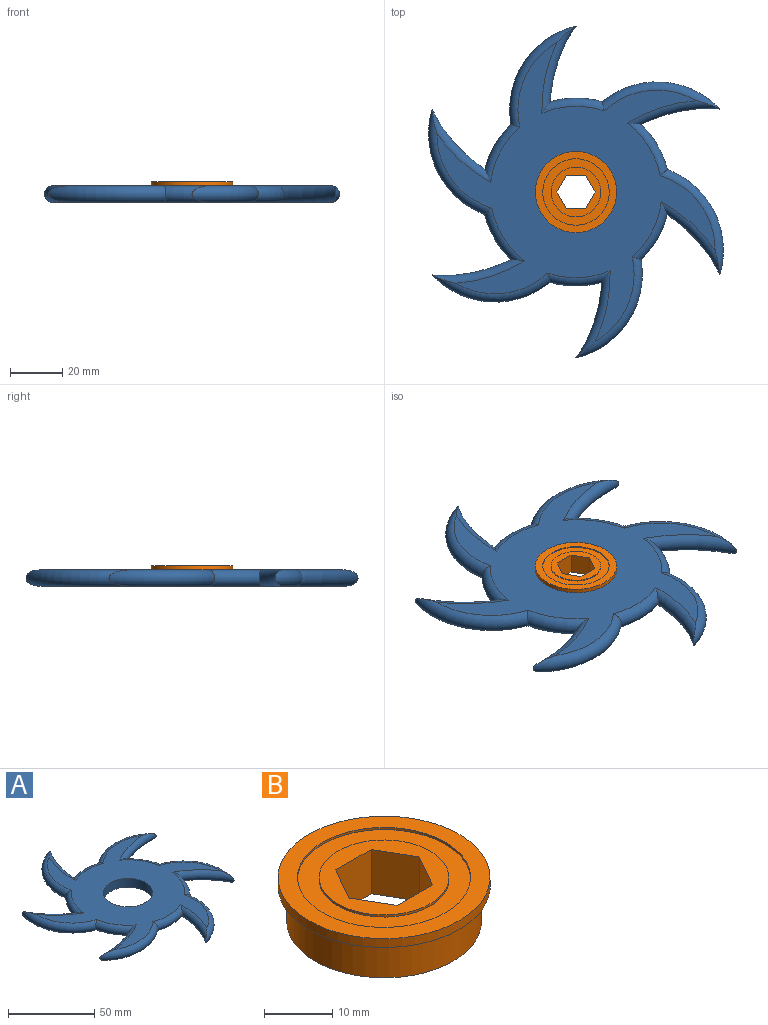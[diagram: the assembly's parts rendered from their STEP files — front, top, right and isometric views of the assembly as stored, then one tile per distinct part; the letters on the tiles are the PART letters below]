
ASSEMBLY  parts=2 mates=1
PART A: 21 faces, bbox 128.9x138.9x6.4 mm
  f0: cylinder r=14.29mm len=28.58mm, axis (0,0,-1), area 570mm2, adj f1,f2
  f1: plane 114.48x106.44mm, normal (0,0,1), area 3978.2mm2, adj f0,f3,f4,f5,f6,f7,f8,f9
  f2: plane 114.48x106.44mm, normal (0,0,-1), area 3978.2mm2, adj f0,f3,f4,f5,f6,f7,f8,f9
  f3: torus R=32.81mm, axis (0,0,1), area 216mm2, adj f1,f2,f4,f5
  f4: torus R=58.98mm, axis (0,0,1), area 299.1mm2, adj f1,f2,f3,f6
  f5: torus R=29.76mm, axis (0,0,1), area 453.4mm2, adj f1,f2,f3,f7
  f6: torus R=29.76mm, axis (0,0,1), area 453.4mm2, adj f1,f2,f4,f8
  f7: torus R=58.98mm, axis (0,0,1), area 299.1mm2, adj f1,f2,f5,f9
  f8: torus R=32.81mm, axis (0,0,1), area 216mm2, adj f1,f2,f6,f10
  f9: torus R=32.81mm, axis (0,0,1), area 216mm2, adj f1,f2,f7,f11
  f10: torus R=58.98mm, axis (0,0,1), area 299.1mm2, adj f1,f2,f8,f12
  f11: torus R=29.76mm, axis (0,0,1), area 453.4mm2, adj f1,f2,f9,f13
  f12: torus R=29.76mm, axis (0,0,1), area 453.4mm2, adj f1,f2,f10,f14
  f13: torus R=58.98mm, axis (0,0,1), area 299.1mm2, adj f1,f2,f11,f15
  f14: torus R=32.81mm, axis (0,0,1), area 216mm2, adj f1,f2,f12,f16
  f15: torus R=32.81mm, axis (0,0,1), area 216mm2, adj f1,f2,f13,f17
  f16: torus R=58.98mm, axis (0,0,1), area 299.1mm2, adj f1,f2,f14,f18
  f17: torus R=29.76mm, axis (0,0,1), area 453.4mm2, adj f1,f2,f15,f19
  f18: torus R=29.76mm, axis (0,0,1), area 453.4mm2, adj f1,f2,f16,f20
  f19: torus R=58.98mm, axis (0,0,1), area 299.1mm2, adj f1,f2,f17,f20
  f20: torus R=32.81mm, axis (0,0,1), area 216mm2, adj f1,f2,f18,f19
PART B: 15 faces, bbox 31.1x31.1x7.9 mm
  f0: cylinder r=12.7mm len=25.4mm, axis (0,0,1), area 30.4mm2, adj f7,f8
  f1: cylinder r=15.56mm len=31.12mm, axis (0,0,1), area 155.2mm2, adj f6,f7
  f2: cylinder r=14.27mm len=28.55mm, axis (0,0,1), area 569.5mm2, adj f5,f6
  f3: cylinder r=9.53mm len=19.05mm, axis (0,0,1), area 22.8mm2, adj f4,f8
  f4: plane 19.05x19.05mm, normal (0,0,1), area 144.9mm2, adj f3,f9,f10,f11,f12,f13,f14
  f5: plane 28.55x28.55mm, normal (0,0,-1), area 500mm2, adj f2,f9,f10,f11,f12,f13,f14
  f6: plane 31.12x31.12mm, normal (0,0,-1), area 120.2mm2, adj f1,f2
  f7: plane 31.12x31.12mm, normal (0,0,1), area 253.7mm2, adj f0,f1
  f8: plane 25.4x25.4mm, normal (0,0,1), area 221.7mm2, adj f0,f3
  f9: plane 7.94x6.36mm, normal (-0.87,-0.5,0), area 58.3mm2, adj f4,f5,f10,f14
  f10: plane 7.94x6.36mm, normal (-0.87,0.5,0), area 58.3mm2, adj f4,f5,f9,f11
  f11: plane 7.94x7.34mm, normal (0,1,0), area 58.3mm2, adj f4,f5,f10,f12
  f12: plane 7.94x6.36mm, normal (0.87,0.5,0), area 58.3mm2, adj f4,f5,f11,f13
  f13: plane 7.94x6.36mm, normal (0.87,-0.5,0), area 58.3mm2, adj f4,f5,f12,f14
  f14: plane 7.94x7.34mm, normal (0,-1,0), area 58.3mm2, adj f4,f5,f9,f13
PLACE A t=(-30.55,3.56,28.61)mm
PLACE B t=(-30.55,3.56,28.61)mm
MATE fastened B.f0 <-> A.f0  axis (0,0,1) through (-30.55,3.56,34.96)mm
